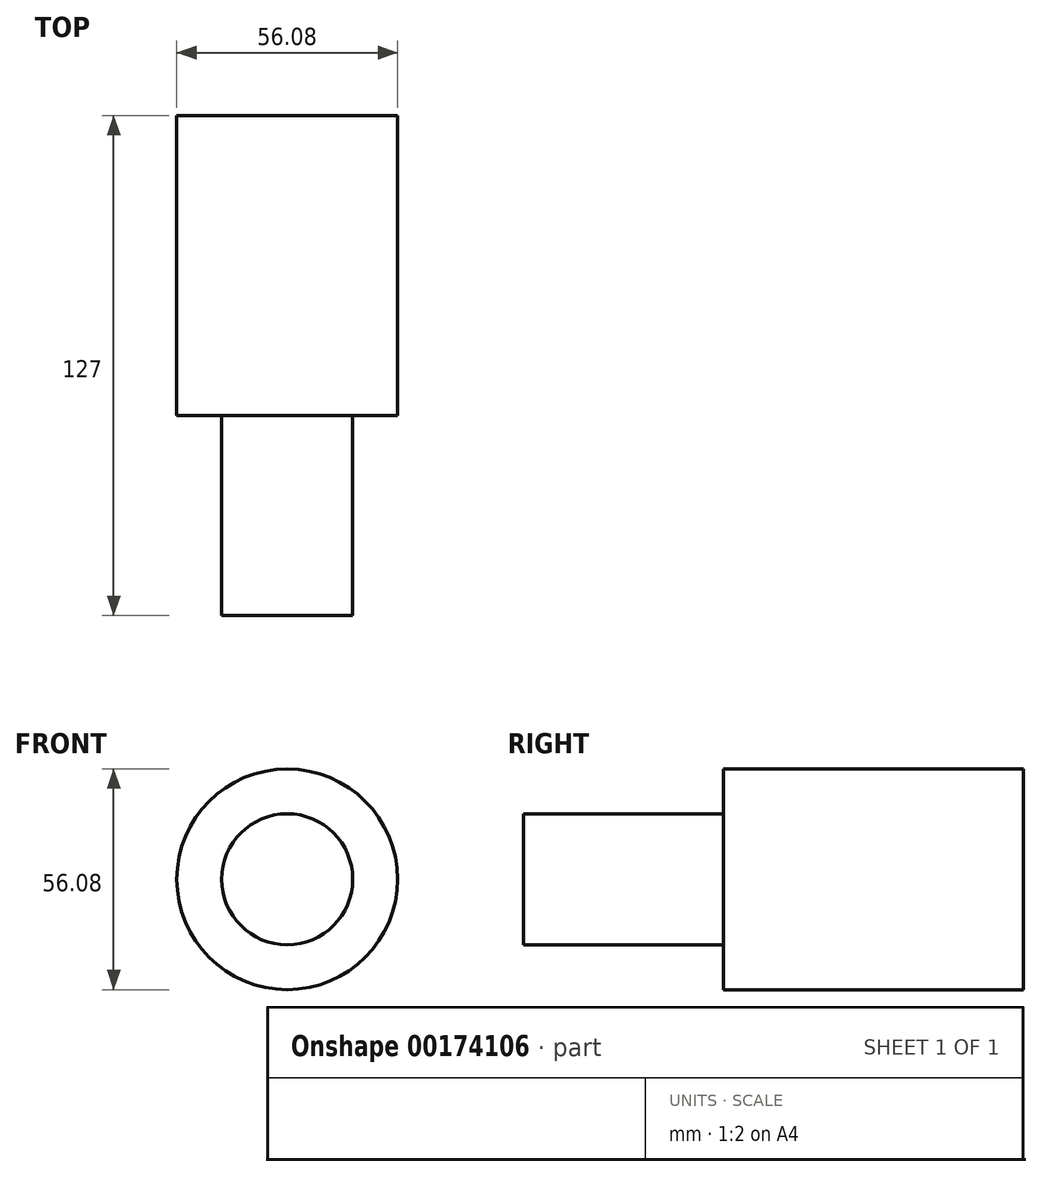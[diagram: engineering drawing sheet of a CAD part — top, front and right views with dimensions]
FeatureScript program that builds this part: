
annotation { "Feature Type Name" : "Feature", "Feature Type Description" : "" }
export const myFeature = defineFeature(function(context is Context, id is Id, definition is map)
    precondition{}
    {
        {
            var Q0;
            Q0=qCreatedBy(makeId("Front.planeOp"),FACE);
            var sketch = newSketch(context, id + "F0", { "sketchPlane" : qUnion([Q0])});
            skCircle(sketch, "E0", {"center": v(0, 0) * mm, "radius": 28.04 * mm});
            skSolve(sketch);
        }
        {
            var Q0;
            Q0 = qSketchRegion(id + "F0", true);
            extrude(context, id + "F1", {"entities" : qUnion([Q0]), "depth" : 76.2 * mm});
        }
        {
            var Q0;
            Q0=qCreatedBy(makeId("Front.planeOp"),FACE);
            var sketch = newSketch(context, id + "F2", { "sketchPlane" : qUnion([Q0])});
            skCircle(sketch, "E1", {"center": v(0, 0) * mm, "radius": 16.65 * mm});
            skSolve(sketch);
        }
        {
            var Q0;
            Q0 = qSketchRegion(id + "F2", true);
            extrude(context, id + "F3", {"entities" : qUnion([Q0]), "operationType" : NewBodyOperationType.ADD, "depth" : 127 * mm});
        }
    });
